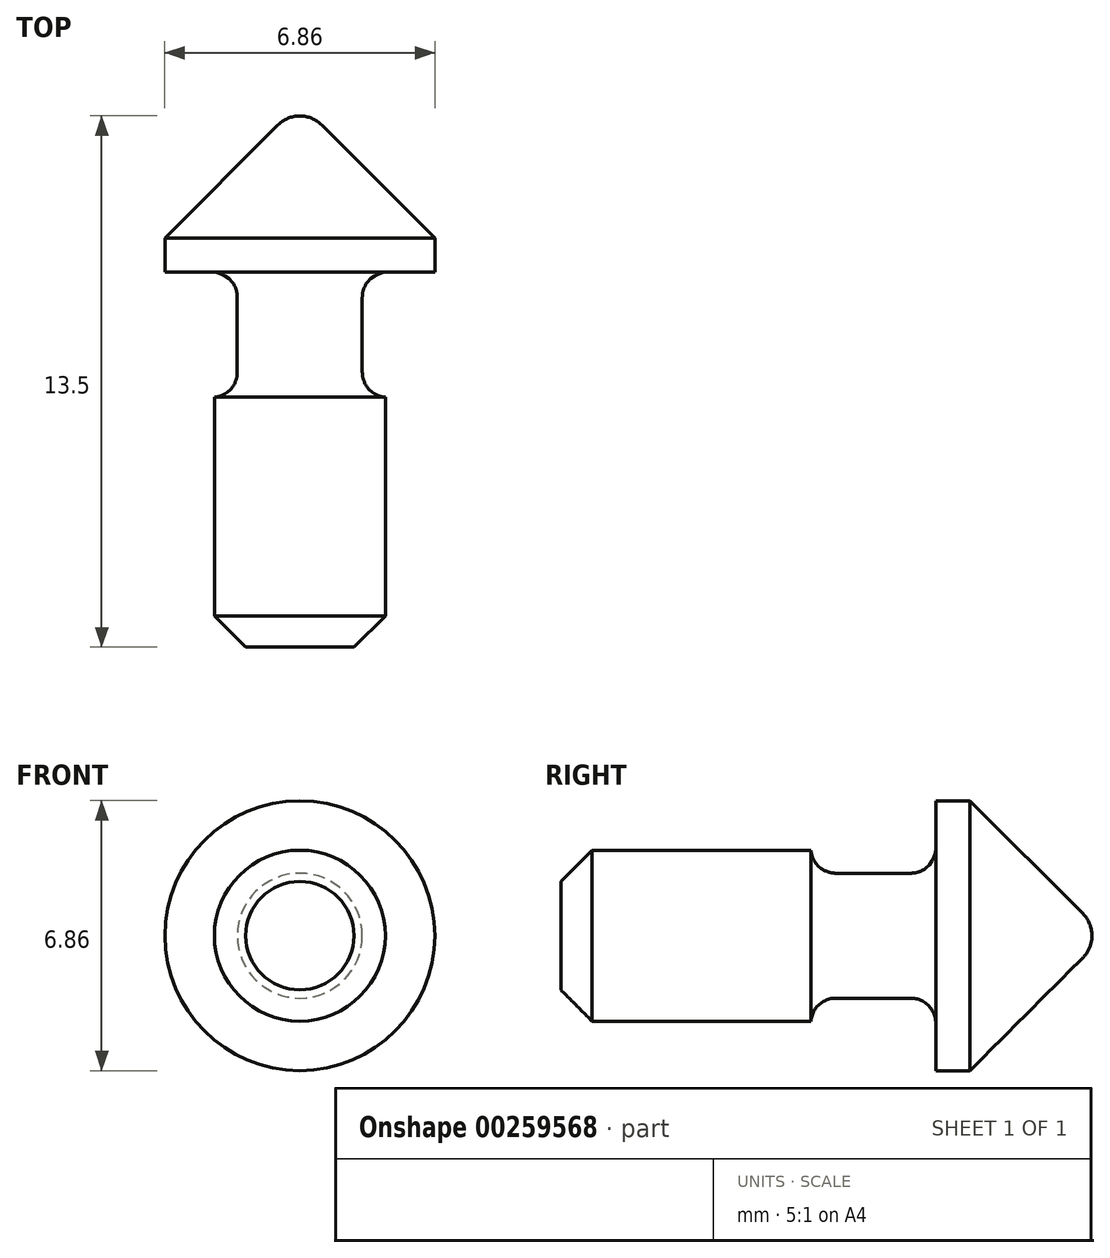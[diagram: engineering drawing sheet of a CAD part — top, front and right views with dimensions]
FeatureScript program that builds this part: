
annotation { "Feature Type Name" : "Feature", "Feature Type Description" : "" }
export const myFeature = defineFeature(function(context is Context, id is Id, definition is map)
    precondition{}
    {
        {
            var Q0;
            Q0=qCreatedBy(makeId("Right.planeOp"),FACE);
            var sketch = newSketch(context, id + "F0", { "sketchPlane" : qUnion([Q0])});
            skLineSegment(sketch, "E0.bottom", {"start": v(2.98, 3.43) * mm, "end": v(3.85, 3.43) * mm});
            skLineSegment(sketch, "E0.left", {"start": v(-6.55, 1.38) * mm, "end": v(-6.55, 0) * mm});
            skPoint(sketch, "E0.middle", {"position": v(0, 0) * mm});
            skPoint(sketch, "E1.centerSnap0", {"position": v(6.55, 0) * mm});
            skLineSegment(sketch, "E2", {"start": v(6.71, 0.56) * mm, "end": v(3.85, 3.43) * mm});
            skPoint(sketch, "E3.MirrorP", {"position": v(7.27, 7.27) * mm});
            skArc(sketch, "E4", {"start": v(6.71, 0.56) * mm, "mid": v(6.88, 0.3) * mm, "end": v(6.95, 0) * mm});
            skLineSegment(sketch, "E5", {"start": v(2.98, 3.43) * mm, "end": v(2.98, 2.22) * mm});
            skLineSegment(sketch, "E6", {"start": v(2.34, 1.59) * mm, "end": v(0.44, 1.59) * mm});
            skLineSegment(sketch, "E7", {"start": v(-0.2, 2.17) * mm, "end": v(-5.75, 2.17) * mm});
            skPoint(sketch, "E8.orphan", {"position": v(-6.55, 3.43) * mm});
            skPoint(sketch, "E9.orphan", {"position": v(6.55, 3.43) * mm});
            skPoint(sketch, "E10.orphan", {"position": v(6.55, -3.43) * mm});
            skPoint(sketch, "E11.orphan", {"position": v(-6.55, -3.43) * mm});
            skPoint(sketch, "E12.orphan", {"position": v(-0.2, 3.43) * mm});
            skLineSegment(sketch, "E13", {"start": v(6.55, 0) * mm, "end": v(-6.55, 0) * mm});
            skPoint(sketch, "E14.visualSharp", {"position": v(2.98, 1.59) * mm});
            skArc(sketch, "E14.filletArc", {"start": v(2.34, 1.59) * mm, "mid": v(2.8, 1.77) * mm, "end": v(2.98, 2.22) * mm});
            skPoint(sketch, "E15.visualSharp", {"position": v(2.98, -1.59) * mm});
            skPoint(sketch, "E16.visualSharp", {"position": v(-0.2, -1.59) * mm});
            skPoint(sketch, "E17.visualSharp", {"position": v(-0.2, 1.59) * mm});
            skArc(sketch, "E17.filletArc", {"start": v(-0.2, 2.17) * mm, "mid": v(0, 1.76) * mm, "end": v(0.44, 1.59) * mm});
            skLineSegment(sketch, "E18", {"start": v(-5.75, 2.17) * mm, "end": v(-6.55, 1.38) * mm});
            skLineSegment(sketch, "E19", {"start": v(-6.55, 0) * mm, "end": v(6.95, 0) * mm});
            skPoint(sketch, "E20.end.orphan", {"position": v(-6.55, -2.17) * mm});
            skPoint(sketch, "E21.trimOffspring.end.orphan", {"position": v(2.98, -3.43) * mm});
            skPoint(sketch, "E22.orphan", {"position": v(-6.55, 2.17) * mm});
            skSolve(sketch);
        }
        {
            var Q0;
            Q0 = qSketchRegion(id + "F0", true);
            var Q1;
            Q1=sQuery(id+"F0.wireOp",EDGE,"E19");
            revolve(context, id + "F1", {"entities" : qUnion([Q0]), "axis" : qUnion([Q1]), "revolveType" : RevolveType.FULL});
        }
    });
